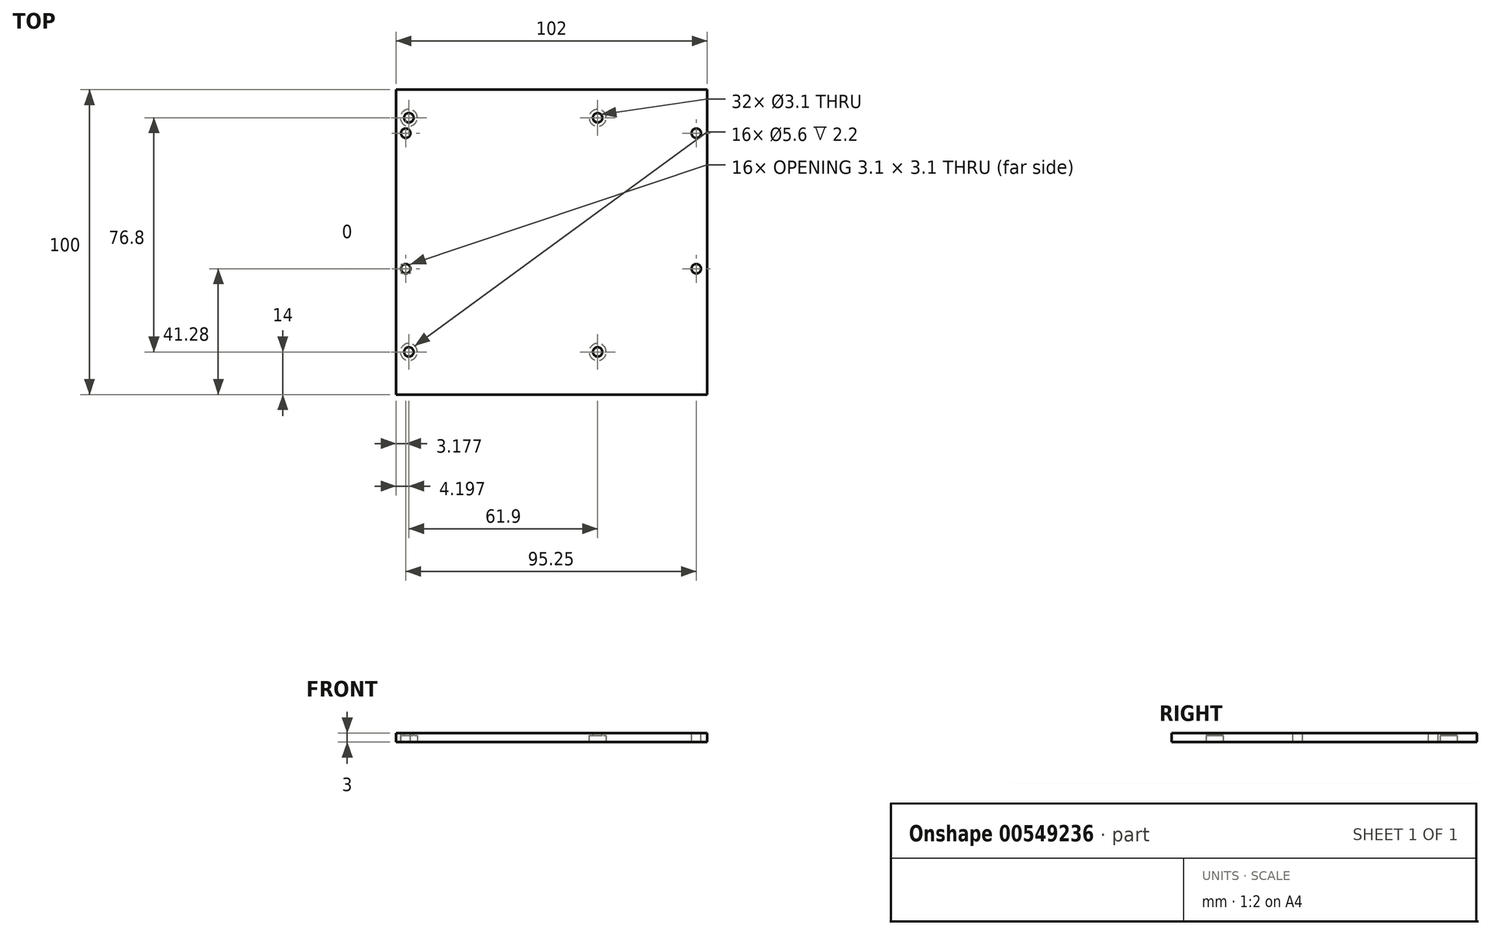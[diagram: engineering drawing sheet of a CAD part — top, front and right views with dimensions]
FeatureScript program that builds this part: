
annotation { "Feature Type Name" : "Feature", "Feature Type Description" : "" }
export const myFeature = defineFeature(function(context is Context, id is Id, definition is map)
    precondition{}
    {
        {
            var Q0;
            Q0=qCreatedBy(makeId("Front.planeOp"),FACE);
            var sketch = newSketch(context, id + "F0", { "sketchPlane" : qUnion([Q0])});
            skLineSegment(sketch, "E0", {"start": v(-51.41, 1.93) * mm, "end": v(50.59, 1.93) * mm});
            skLineSegment(sketch, "E1", {"start": v(50.59, 1.93) * mm, "end": v(50.59, -1.07) * mm});
            skLineSegment(sketch, "E2", {"start": v(-51.41, -1.07) * mm, "end": v(-51.41, 1.93) * mm});
            skLineSegment(sketch, "E3", {"start": v(-51.41, -1.07) * mm, "end": v(50.59, -1.07) * mm});
            skSolve(sketch);
        }
        {
            var Q0;
            Q0=makeQuery(id+"F0.imprint","IMPRINT",FACE,{"disambiguationData":[TD([[makeQuery(id+"F0.imprint","IMPRINT",EDGE,{"derivedFrom":sQuery(id+"F0.wireOp",EDGE,"E0")}),-1.0]])]});
            extrude(context, id + "F1", {"entities" : qUnion([Q0]), "endBound" : BoundingType.SYMMETRIC, "oppositeDirection" : true, "depth" : 100 * mm, "offsetDistance" : 25 * mm});
        }
        {
            var Q0;
            Q0=makeQuery(id+"F1.opExtrude","SWEPT_FACE",FACE,{"disambiguationData":[OSD([sQuery(id+"F0.wireOp",EDGE,"E0")])]});
            var sketch = newSketch(context, id + "F2", { "sketchPlane" : qUnion([Q0])});
            skCircle(sketch, "E4", {"center": v(-47.21, -36) * mm, "radius": 1.55 * mm});
            skCircle(sketch, "E5", {"center": v(-47.21, 40.8) * mm, "radius": 1.55 * mm});
            skCircle(sketch, "E6", {"center": v(14.69, 40.8) * mm, "radius": 1.55 * mm});
            skCircle(sketch, "E7", {"center": v(14.69, -36) * mm, "radius": 1.55 * mm});
            skCircle(sketch, "E8", {"center": v(-48.23, -8.72) * mm, "radius": 1.55 * mm});
            skCircle(sketch, "E9", {"center": v(-48.23, 35.73) * mm, "radius": 1.55 * mm});
            skCircle(sketch, "E10", {"center": v(47.02, 35.73) * mm, "radius": 1.55 * mm});
            skCircle(sketch, "E11", {"center": v(47.02, -8.72) * mm, "radius": 1.55 * mm});
            skSolve(sketch);
        }
        {
            var Q0;
            Q0=makeQuery(id+"F2.imprint","IMPRINT",FACE,{"disambiguationData":[TD([[makeQuery(id+"F2.imprint","IMPRINT",EDGE,{"derivedFrom":sQuery(id+"F2.wireOp",EDGE,"E5")}),1.0]])]});
            var Q1;
            Q1=makeQuery(id+"F2.imprint","IMPRINT",FACE,{"disambiguationData":[TD([[makeQuery(id+"F2.imprint","IMPRINT",EDGE,{"derivedFrom":sQuery(id+"F2.wireOp",EDGE,"E6")}),1.0]])]});
            var Q2;
            Q2=makeQuery(id+"F2.imprint","IMPRINT",FACE,{"disambiguationData":[TD([[makeQuery(id+"F2.imprint","IMPRINT",EDGE,{"derivedFrom":sQuery(id+"F2.wireOp",EDGE,"E7")}),1.0]])]});
            var Q3;
            Q3=makeQuery(id+"F2.imprint","IMPRINT",FACE,{"disambiguationData":[TD([[makeQuery(id+"F2.imprint","IMPRINT",EDGE,{"derivedFrom":sQuery(id+"F2.wireOp",EDGE,"E4")}),1.0]])]});
            var Q4;
            Q4=makeQuery(id+"F2.imprint","IMPRINT",FACE,{"disambiguationData":[TD([[makeQuery(id+"F2.imprint","IMPRINT",EDGE,{"derivedFrom":sQuery(id+"F2.wireOp",EDGE,"E9")}),1.0]])]});
            var Q5;
            Q5=makeQuery(id+"F2.imprint","IMPRINT",FACE,{"disambiguationData":[TD([[makeQuery(id+"F2.imprint","IMPRINT",EDGE,{"derivedFrom":sQuery(id+"F2.wireOp",EDGE,"E8")}),1.0]])]});
            var Q6;
            Q6=makeQuery(id+"F2.imprint","IMPRINT",FACE,{"disambiguationData":[TD([[makeQuery(id+"F2.imprint","IMPRINT",EDGE,{"derivedFrom":sQuery(id+"F2.wireOp",EDGE,"E11")}),1.0]])]});
            var Q7;
            Q7=makeQuery(id+"F2.imprint","IMPRINT",FACE,{"disambiguationData":[TD([[makeQuery(id+"F2.imprint","IMPRINT",EDGE,{"derivedFrom":sQuery(id+"F2.wireOp",EDGE,"E10")}),1.0]])]});
            extrude(context, id + "F3", {"entities" : qUnion([Q0, Q1, Q2, Q3, Q4, Q5, Q6, Q7]), "operationType" : NewBodyOperationType.REMOVE, "endBound" : BoundingType.UP_TO_NEXT, "oppositeDirection" : true, "depth" : 25 * mm, "offsetDistance" : 25 * mm});
        }
        {
            var Q0;
            Q0=makeQuery(id+"F1.opExtrude","SWEPT_FACE",FACE,{"disambiguationData":[OSD([sQuery(id+"F0.wireOp",EDGE,"E3")])]});
            var sketch = newSketch(context, id + "F4", { "sketchPlane" : qUnion([Q0])});
            skCircle(sketch, "E12", {"center": v(-47.21, 36) * mm, "radius": 2.8 * mm});
            skCircle(sketch, "E13", {"center": v(14.69, 36) * mm, "radius": 2.8 * mm});
            skCircle(sketch, "E14", {"center": v(-47.21, -40.8) * mm, "radius": 2.8 * mm});
            skCircle(sketch, "E15", {"center": v(14.69, -40.8) * mm, "radius": 2.8 * mm});
            skSolve(sketch);
        }
        {
            var Q0;
            Q0=makeQuery(id+"F4.imprint","IMPRINT",FACE,{"disambiguationData":[TD([[makeQuery(id+"F4.imprint","IMPRINT",EDGE,{"derivedFrom":sQuery(id+"F4.wireOp",EDGE,"E12")}),1.0]])]});
            var Q1;
            Q1=makeQuery(id+"F4.imprint","IMPRINT",FACE,{"disambiguationData":[TD([[makeQuery(id+"F4.imprint","IMPRINT",EDGE,{"derivedFrom":sQuery(id+"F4.wireOp",EDGE,"E13")}),1.0]])]});
            var Q2;
            Q2=makeQuery(id+"F4.imprint","IMPRINT",FACE,{"disambiguationData":[TD([[makeQuery(id+"F4.imprint","IMPRINT",EDGE,{"derivedFrom":sQuery(id+"F4.wireOp",EDGE,"E14")}),1.0]])]});
            var Q3;
            Q3=makeQuery(id+"F4.imprint","IMPRINT",FACE,{"disambiguationData":[TD([[makeQuery(id+"F4.imprint","IMPRINT",EDGE,{"derivedFrom":sQuery(id+"F4.wireOp",EDGE,"E15")}),1.0]])]});
            extrude(context, id + "F5", {"entities" : qUnion([Q0, Q1, Q2, Q3]), "operationType" : NewBodyOperationType.REMOVE, "oppositeDirection" : true, "depth" : 2.2 * mm, "offsetDistance" : 25 * mm});
        }
    });
